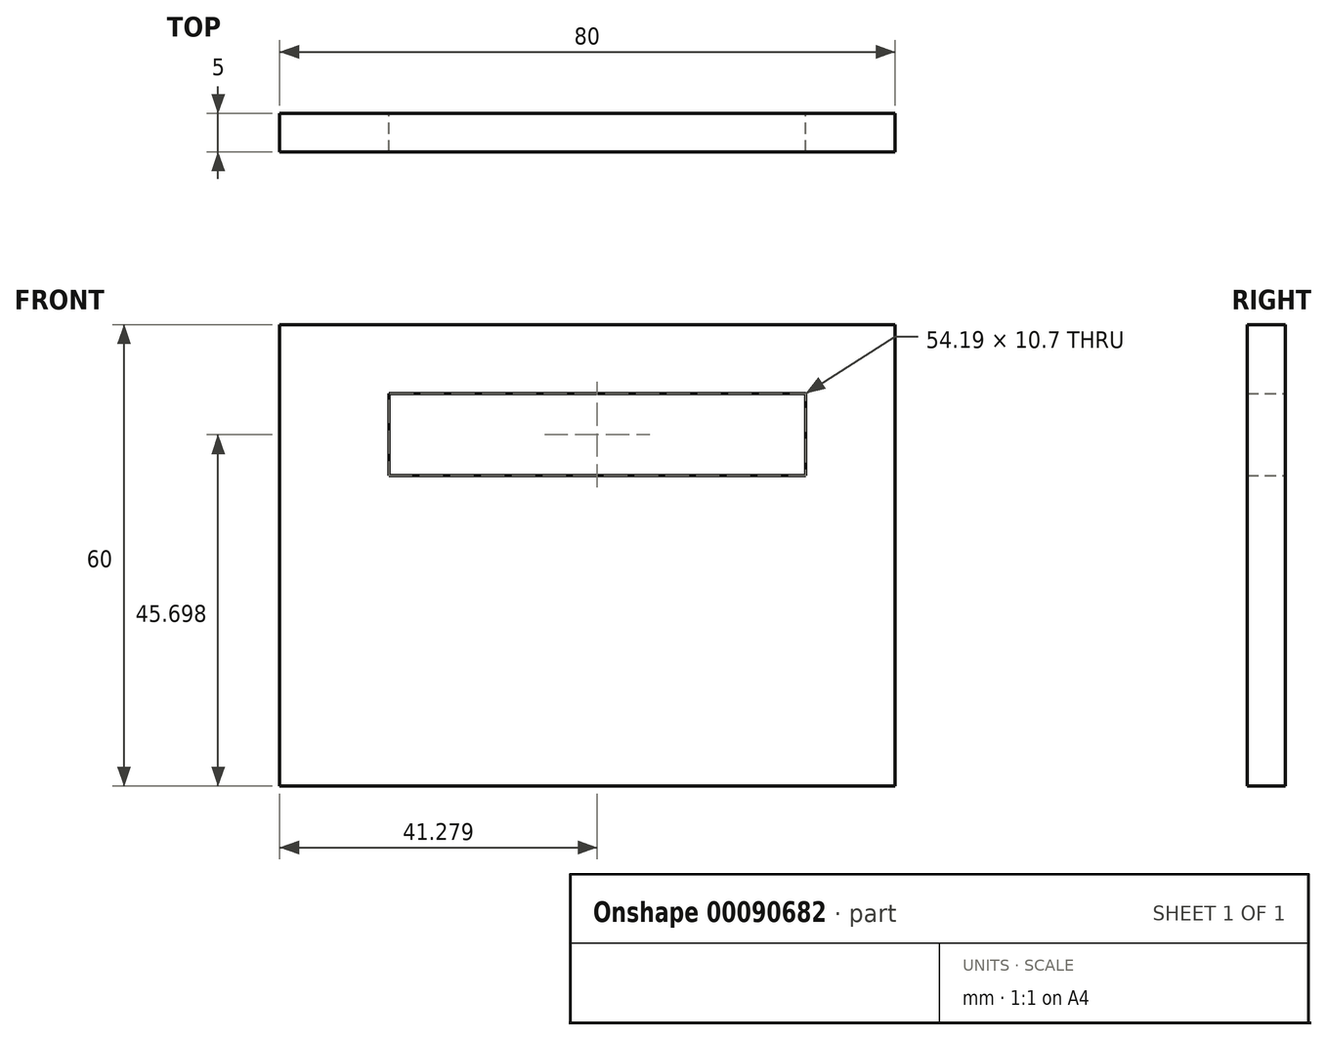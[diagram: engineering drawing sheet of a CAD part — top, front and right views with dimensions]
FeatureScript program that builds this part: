
annotation { "Feature Type Name" : "Feature", "Feature Type Description" : "" }
export const myFeature = defineFeature(function(context is Context, id is Id, definition is map)
    precondition{}
    {
        {
            var Q0;
            Q0=qCreatedBy(makeId("Front.planeOp"),FACE);
            var sketch = newSketch(context, id + "F0", { "sketchPlane" : qUnion([Q0])});
            skLineSegment(sketch, "E0.bottom", {"start": v(40, 30) * mm, "end": v(-40, 30) * mm});
            skLineSegment(sketch, "E0.top", {"start": v(40, -30) * mm, "end": v(-40, -30) * mm});
            skLineSegment(sketch, "E0.left", {"start": v(40, 30) * mm, "end": v(40, -30) * mm});
            skLineSegment(sketch, "E0.right", {"start": v(-40, 30) * mm, "end": v(-40, -30) * mm});
            skPoint(sketch, "E0.middle", {"position": v(0, 0) * mm});
            skLineSegment(sketch, "E1.bottom", {"start": v(-25.81, 10.35) * mm, "end": v(28.37, 10.35) * mm});
            skLineSegment(sketch, "E1.top", {"start": v(-25.81, 21.05) * mm, "end": v(28.37, 21.05) * mm});
            skLineSegment(sketch, "E1.left", {"start": v(-25.81, 10.35) * mm, "end": v(-25.81, 21.05) * mm});
            skLineSegment(sketch, "E1.right", {"start": v(28.37, 10.35) * mm, "end": v(28.37, 21.05) * mm});
            skSolve(sketch);
        }
        {
            var Q0;
            Q0 = qSketchRegion(id + "F0", true);
            extrude(context, id + "F1", {"entities" : qUnion([Q0]), "depth" : 5 * mm});
        }
    });
